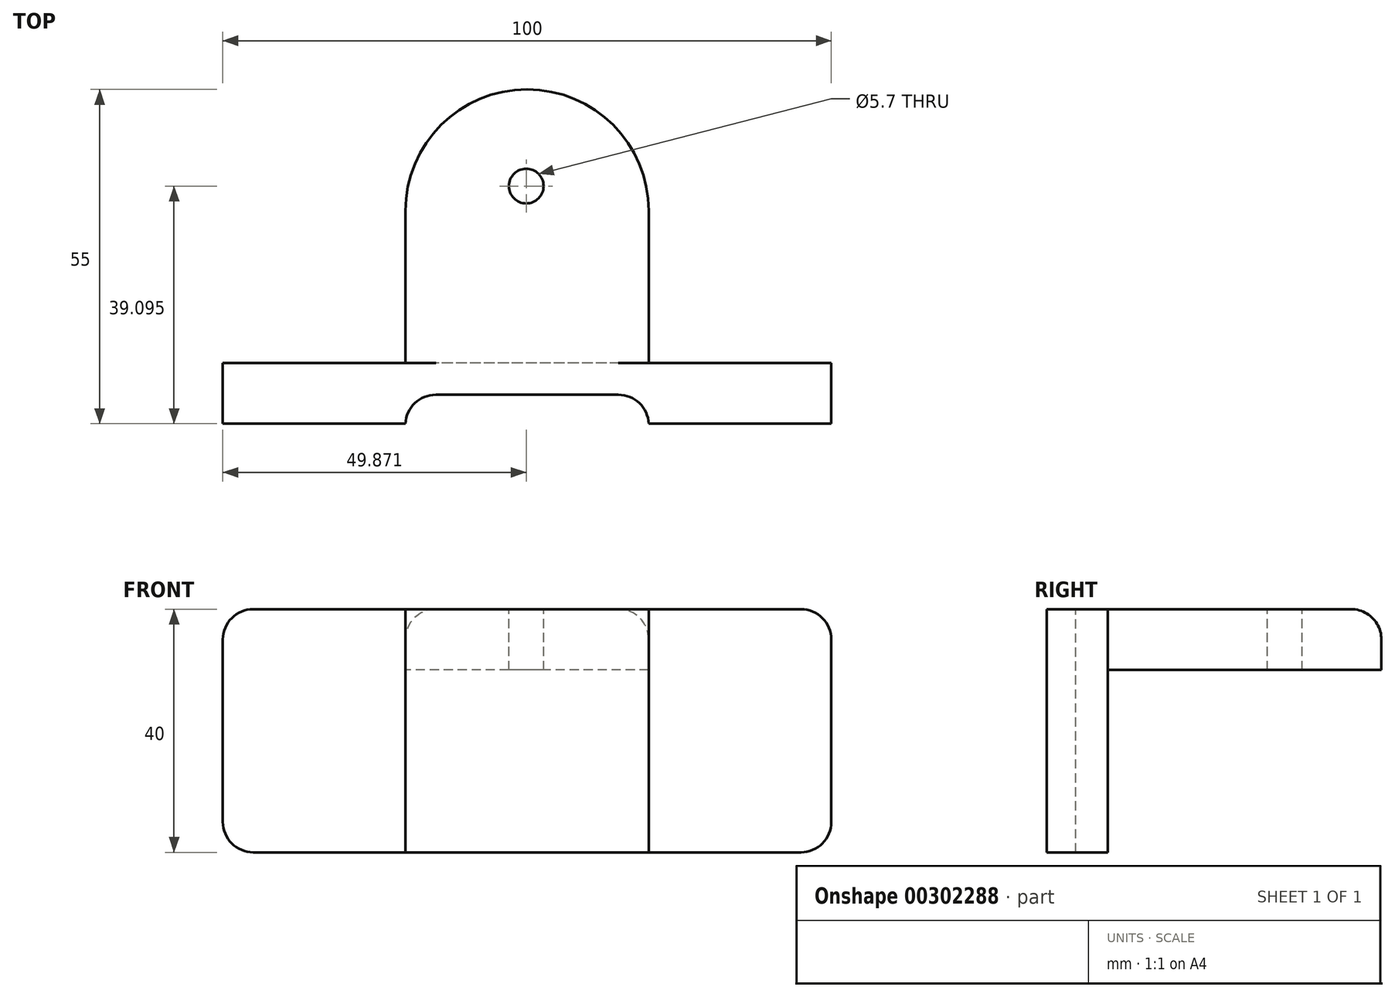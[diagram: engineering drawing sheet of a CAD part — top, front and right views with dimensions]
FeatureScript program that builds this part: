
annotation { "Feature Type Name" : "Feature", "Feature Type Description" : "" }
export const myFeature = defineFeature(function(context is Context, id is Id, definition is map)
    precondition{}
    {
        {
            var Q0;
            Q0=qCreatedBy(makeId("Front.planeOp"),FACE);
            var sketch = newSketch(context, id + "F0", { "sketchPlane" : qUnion([Q0])});
            skLineSegment(sketch, "E0.bottom", {"start": v(0, 0) * mm, "end": v(-100, 0) * mm});
            skLineSegment(sketch, "E0.top", {"start": v(0, 40) * mm, "end": v(-100, 40) * mm});
            skLineSegment(sketch, "E0.left", {"start": v(0, 0) * mm, "end": v(0, 40) * mm});
            skLineSegment(sketch, "E0.right", {"start": v(-100, 0) * mm, "end": v(-100, 40) * mm});
            skSolve(sketch);
        }
        {
            var Q0;
            Q0 = qSketchRegion(id + "F0", true);
            extrude(context, id + "F1", {"entities" : qUnion([Q0]), "depth" : 10 * mm});
        }
        {
            var Q0;
            Q0=makeQuery(id+"F1.opExtrude","SWEPT_FACE",FACE,{"disambiguationData":[OSD([sQuery(id+"F0.wireOp",EDGE,"E0.top")])]});
            var sketch = newSketch(context, id + "F2", { "sketchPlane" : qUnion([Q0])});
            skLineSegment(sketch, "E1", {"start": v(-70, 0) * mm, "end": v(-70, 25) * mm});
            skArc(sketch, "E2", {"start": v(-30, 25) * mm, "mid": v(-50, 45) * mm, "end": v(-70, 25) * mm});
            skLineSegment(sketch, "E3", {"start": v(-30, 25) * mm, "end": v(-30, 0) * mm});
            skPoint(sketch, "E4.endSnap0", {"position": v(-50, -10) * mm});
            skLineSegment(sketch, "E5", {"start": v(-70, 0) * mm, "end": v(-70, -10) * mm});
            skLineSegment(sketch, "E6", {"start": v(-30, 0) * mm, "end": v(-30, -10) * mm});
            skLineSegment(sketch, "E7", {"start": v(-30, -10) * mm, "end": v(-70, -10) * mm});
            skSolve(sketch);
        }
        {
            var Q0;
            Q0 = qSketchRegion(id + "F2", true);
            var Q1;
            {var subQ0=sQuery(id+"F2.wireOp",EDGE,"E1");Q1=makeQuery(id+"F2.imprint","IMPRINT",FACE,{"disambiguationData":[TD([[makeQuery(id+"F2.imprint","IMPRINT",EDGE,{"derivedFrom":subQ0}),-1.0]])]});}
            extrude(context, id + "F3", {"entities" : qUnion([Q0, Q1]), "operationType" : NewBodyOperationType.ADD, "oppositeDirection" : true, "depth" : 10 * mm});
        }
        {
            var Q0;
            Q0=makeQuery(id+"F3.boolean.opBoolean","MERGE",FACE,{"derivedFrom":[makeQuery(id+"F1.opExtrude","SWEPT_FACE",FACE,{"disambiguationData":[OSD([sQuery(id+"F0.wireOp",EDGE,"E0.top")])]}),makeQuery(id+"F3.opExtrude","CAP_FACE",FACE,{"disambiguationData":[OSD([sQuery(id+"F2.wireOp",EDGE,"E1"),sQuery(id+"F2.wireOp",EDGE,"E2"),sQuery(id+"F2.wireOp",EDGE,"E3"),sQuery(id+"F2.wireOp",EDGE,"E5"),sQuery(id+"F2.wireOp",EDGE,"E6"),sQuery(id+"F2.wireOp",EDGE,"E7")])],"isStart":true})]});
            var sketch = newSketch(context, id + "F4", { "sketchPlane" : qUnion([Q0])});
            skLineSegment(sketch, "E8.bottom", {"start": v(-70, -10) * mm, "end": v(-30, -10) * mm});
            skLineSegment(sketch, "E8.top", {"start": v(-70, -7) * mm, "end": v(-30, -7) * mm});
            skLineSegment(sketch, "E8.left", {"start": v(-70, -10) * mm, "end": v(-70, -7) * mm});
            skLineSegment(sketch, "E8.right", {"start": v(-30, -10) * mm, "end": v(-30, -7) * mm});
            skSolve(sketch);
        }
        {
            var Q0;
            Q0=makeQuery(id+"F4.imprint","IMPRINT",FACE,{"disambiguationData":[TD([[makeQuery(id+"F4.imprint","IMPRINT",EDGE,{"derivedFrom":sQuery(id+"F4.wireOp",EDGE,"E8.bottom")}),-1.0]])]});
            extrude(context, id + "F5", {"entities" : qUnion([Q0]), "operationType" : NewBodyOperationType.REMOVE, "endBound" : BoundingType.THROUGH_ALL, "depth" : 25 * mm});
        }
        {
            var Q0;
            Q0=makeQuery(id+"F3.boolean.opBoolean","MERGE",FACE,{"derivedFrom":[makeQuery(id+"F1.opExtrude","SWEPT_FACE",FACE,{"disambiguationData":[OSD([sQuery(id+"F0.wireOp",EDGE,"E0.top")])]}),makeQuery(id+"F3.opExtrude","CAP_FACE",FACE,{"disambiguationData":[OSD([sQuery(id+"F2.wireOp",EDGE,"E1"),sQuery(id+"F2.wireOp",EDGE,"E2"),sQuery(id+"F2.wireOp",EDGE,"E3"),sQuery(id+"F2.wireOp",EDGE,"E5"),sQuery(id+"F2.wireOp",EDGE,"E6"),sQuery(id+"F2.wireOp",EDGE,"E7")])],"isStart":true})]});
            var sketch = newSketch(context, id + "F6", { "sketchPlane" : qUnion([Q0])});
            skLineSegment(sketch, "E9.bottom", {"start": v(-70, -10) * mm, "end": v(-30, -10) * mm});
            skLineSegment(sketch, "E9.top", {"start": v(-70, -5.24) * mm, "end": v(-30, -5.24) * mm});
            skLineSegment(sketch, "E9.left", {"start": v(-70, -10) * mm, "end": v(-70, -5.24) * mm});
            skLineSegment(sketch, "E9.right", {"start": v(-30, -10) * mm, "end": v(-30, -5.24) * mm});
            skSolve(sketch);
        }
        {
            var Q0;
            Q0 = qSketchRegion(id + "F6", true);
            extrude(context, id + "F7", {"entities" : qUnion([Q0]), "operationType" : NewBodyOperationType.REMOVE, "endBound" : BoundingType.THROUGH_ALL, "oppositeDirection" : true, "depth" : 25 * mm});
        }
        {
            var Q0;
            Q0=makeQuery(id+"F3.boolean.opBoolean","MERGE",FACE,{"derivedFrom":[makeQuery(id+"F1.opExtrude","SWEPT_FACE",FACE,{"disambiguationData":[OSD([sQuery(id+"F0.wireOp",EDGE,"E0.top")])]}),makeQuery(id+"F3.opExtrude","CAP_FACE",FACE,{"disambiguationData":[OSD([sQuery(id+"F2.wireOp",EDGE,"E1"),sQuery(id+"F2.wireOp",EDGE,"E2"),sQuery(id+"F2.wireOp",EDGE,"E3"),sQuery(id+"F2.wireOp",EDGE,"E5"),sQuery(id+"F2.wireOp",EDGE,"E6"),sQuery(id+"F2.wireOp",EDGE,"E7")])],"isStart":true})]});
            var sketch = newSketch(context, id + "F8", { "sketchPlane" : qUnion([Q0])});
            skCircle(sketch, "E10", {"center": v(-50.13, 29.1) * mm, "radius": 2.85 * mm});
            skSolve(sketch);
        }
        {
            var Q0;
            Q0 = qSketchRegion(id + "F8", true);
            extrude(context, id + "F9", {"entities" : qUnion([Q0]), "operationType" : NewBodyOperationType.REMOVE, "endBound" : BoundingType.THROUGH_ALL, "oppositeDirection" : true, "depth" : 25 * mm});
        }
        {
            var Q0;
            Q0=makeQuery(id+"F3.opExtrude","CAP_EDGE",EDGE,{"disambiguationData":[OSD([sQuery(id+"F2.wireOp",EDGE,"E1"),sQuery(id+"F2.wireOp",EDGE,"E5")])],"isStart":true});
            fillet(context, id + "F10", {"entities" : qUnion([Q0]), "radius" : 5 * mm, "tangentPropagation" : true, "allowEdgeOverflow" : false});
        }
        {
            var Q0;
            Q0=makeQuery(id+"F7.boolean.opBoolean","COPY",EDGE,{"derivedFrom":makeQuery(id+"F7.opExtrude","SWEPT_EDGE",EDGE,{"disambiguationData":[OSD([sQuery(id+"F6.wireOp",EDGE,"E9.top"),sQuery(id+"F6.wireOp",EDGE,"E9.right")])]})});
            fillet(context, id + "F11", {"entities" : qUnion([Q0]), "radius" : 5 * mm, "tangentPropagation" : true, "allowEdgeOverflow" : false});
        }
        {
            var Q0;
            Q0=makeQuery(id+"F7.boolean.opBoolean","COPY",EDGE,{"derivedFrom":makeQuery(id+"F7.opExtrude","SWEPT_EDGE",EDGE,{"disambiguationData":[OSD([sQuery(id+"F6.wireOp",EDGE,"E9.top"),sQuery(id+"F6.wireOp",EDGE,"E9.left")])]})});
            fillet(context, id + "F12", {"entities" : qUnion([Q0]), "radius" : 5 * mm, "tangentPropagation" : true, "allowEdgeOverflow" : false});
        }
        {
            var Q0;
            Q0=makeQuery(id+"F1.opExtrude","SWEPT_EDGE",EDGE,{"disambiguationData":[OSD([sQuery(id+"F0.wireOp",EDGE,"E0.top"),sQuery(id+"F0.wireOp",EDGE,"E0.right")])]});
            fillet(context, id + "F13", {"entities" : qUnion([Q0]), "radius" : 5 * mm, "tangentPropagation" : true, "allowEdgeOverflow" : false});
        }
        {
            var Q0;
            Q0=makeQuery(id+"F1.opExtrude","SWEPT_EDGE",EDGE,{"disambiguationData":[OSD([sQuery(id+"F0.wireOp",EDGE,"E0.bottom"),sQuery(id+"F0.wireOp",EDGE,"E0.right")])]});
            fillet(context, id + "F14", {"entities" : qUnion([Q0]), "radius" : 5 * mm, "tangentPropagation" : true, "allowEdgeOverflow" : false});
        }
        {
            var Q0;
            Q0=makeQuery(id+"F1.opExtrude","SWEPT_EDGE",EDGE,{"disambiguationData":[OSD([sQuery(id+"F0.wireOp",EDGE,"E0.bottom"),sQuery(id+"F0.wireOp",EDGE,"E0.left")])]});
            fillet(context, id + "F15", {"entities" : qUnion([Q0]), "radius" : 5 * mm, "tangentPropagation" : true, "allowEdgeOverflow" : false});
        }
        {
            var Q0;
            Q0=makeQuery(id+"F1.opExtrude","SWEPT_EDGE",EDGE,{"disambiguationData":[OSD([sQuery(id+"F0.wireOp",EDGE,"E0.top"),sQuery(id+"F0.wireOp",EDGE,"E0.left")])]});
            fillet(context, id + "F16", {"entities" : qUnion([Q0]), "radius" : 5 * mm, "tangentPropagation" : true, "allowEdgeOverflow" : false});
        }
    });
